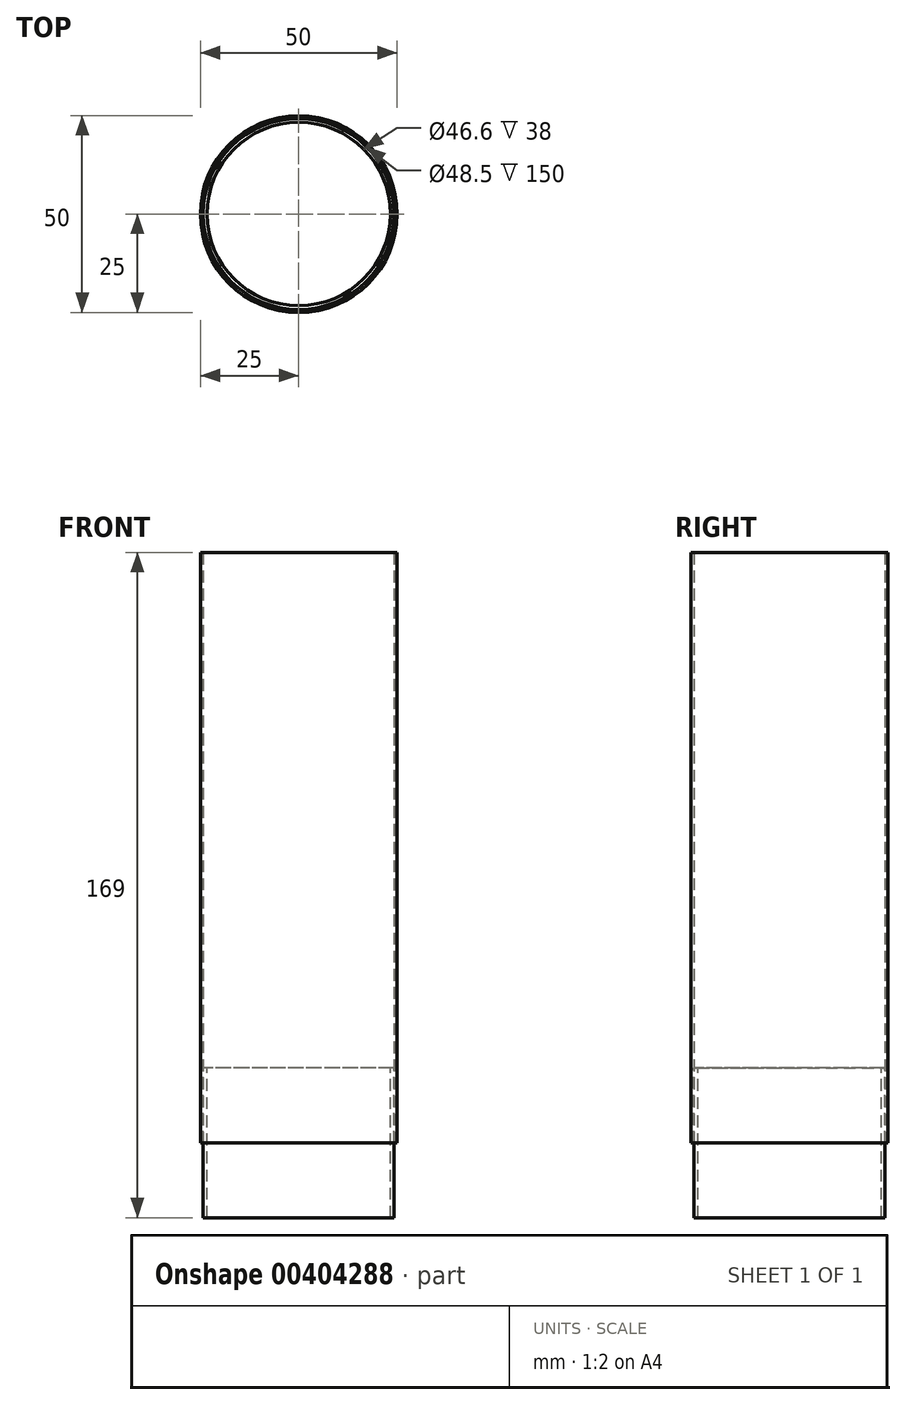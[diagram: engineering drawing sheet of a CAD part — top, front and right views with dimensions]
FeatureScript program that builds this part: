
annotation { "Feature Type Name" : "Feature", "Feature Type Description" : "" }
export const myFeature = defineFeature(function(context is Context, id is Id, definition is map)
    precondition{}
    {
        {
            var Q0;
            Q0=qCreatedBy(makeId("Top.planeOp"),FACE);
            var sketch = newSketch(context, id + "F0", { "sketchPlane" : qUnion([Q0])});
            skCircle(sketch, "E0", {"center": v(0, 0) * mm, "radius": 24.25 * mm});
            skCircle(sketch, "E1", {"center": v(0, 0) * mm, "radius": 25 * mm});
            skCircle(sketch, "E2", {"center": v(0, 0) * mm, "radius": 23.3 * mm});
            skSolve(sketch);
        }
        {
            var Q0;
            Q0=makeQuery(id+"F0.imprint","IMPRINT",FACE,{"disambiguationData":[TD([[makeQuery(id+"F0.imprint","IMPRINT",EDGE,{"derivedFrom":sQuery(id+"F0.wireOp",EDGE,"E0")}),-1.0]])]});
            extrude(context, id + "F1", {"entities" : qUnion([Q0]), "depth" : 150 * mm});
        }
        {
            var Q0;
            Q0=makeQuery(id+"F0.imprint","IMPRINT",FACE,{"disambiguationData":[TD([[makeQuery(id+"F0.imprint","IMPRINT",EDGE,{"derivedFrom":sQuery(id+"F0.wireOp",EDGE,"E0")}),1.0]])]});
            var Q1;
            Q1=sQuery(id+"F0.wireOp",EDGE,"E1");
            var Q2;
            Q2=sQuery(id+"F0.wireOp",EDGE,"E2");
            extrude(context, id + "F2", {"entities" : qUnion([Q0]), "surfaceEntities" : qUnion([Q1, Q2]), "oppositeDirection" : true, "depth" : 19 * mm, "hasSecondDirection" : true, "secondDirectionOppositeDirection" : false, "secondDirectionDepth" : 19 * mm});
        }
    });
